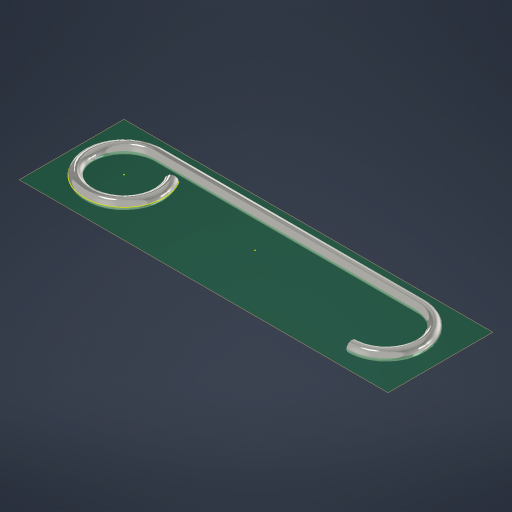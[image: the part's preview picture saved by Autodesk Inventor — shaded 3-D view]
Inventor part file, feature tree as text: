
AUTODESK INVENTOR PART (.ipt)
format: ipt  version: 2024 (Build 280153000, 153)  size: 281,088 bytes
history: native  units: mm
features: other x5, sweep x1, plane x1, sketch x1
ambient origin geometry x8: Origin, YZ Plane, XZ Plane, XY Plane, X Axis, Y Axis, Z Axis, Center Point
bodies: Body1 (feature_tree)
feature tree (8):
  other  "Sólido1"
  sweep  "Barrido1"
  plane  "Plano de trabajo3"
  sketch  "Boceto5"  dims[d3=2.0mm d4=4.0mm d5=0.0mm d6=0.0mm]
  other  "Punto de trabajo8"
  other  "Punto de trabajo9"
  other  "Punto de trabajo10"
  other  "Punto de trabajo11"
